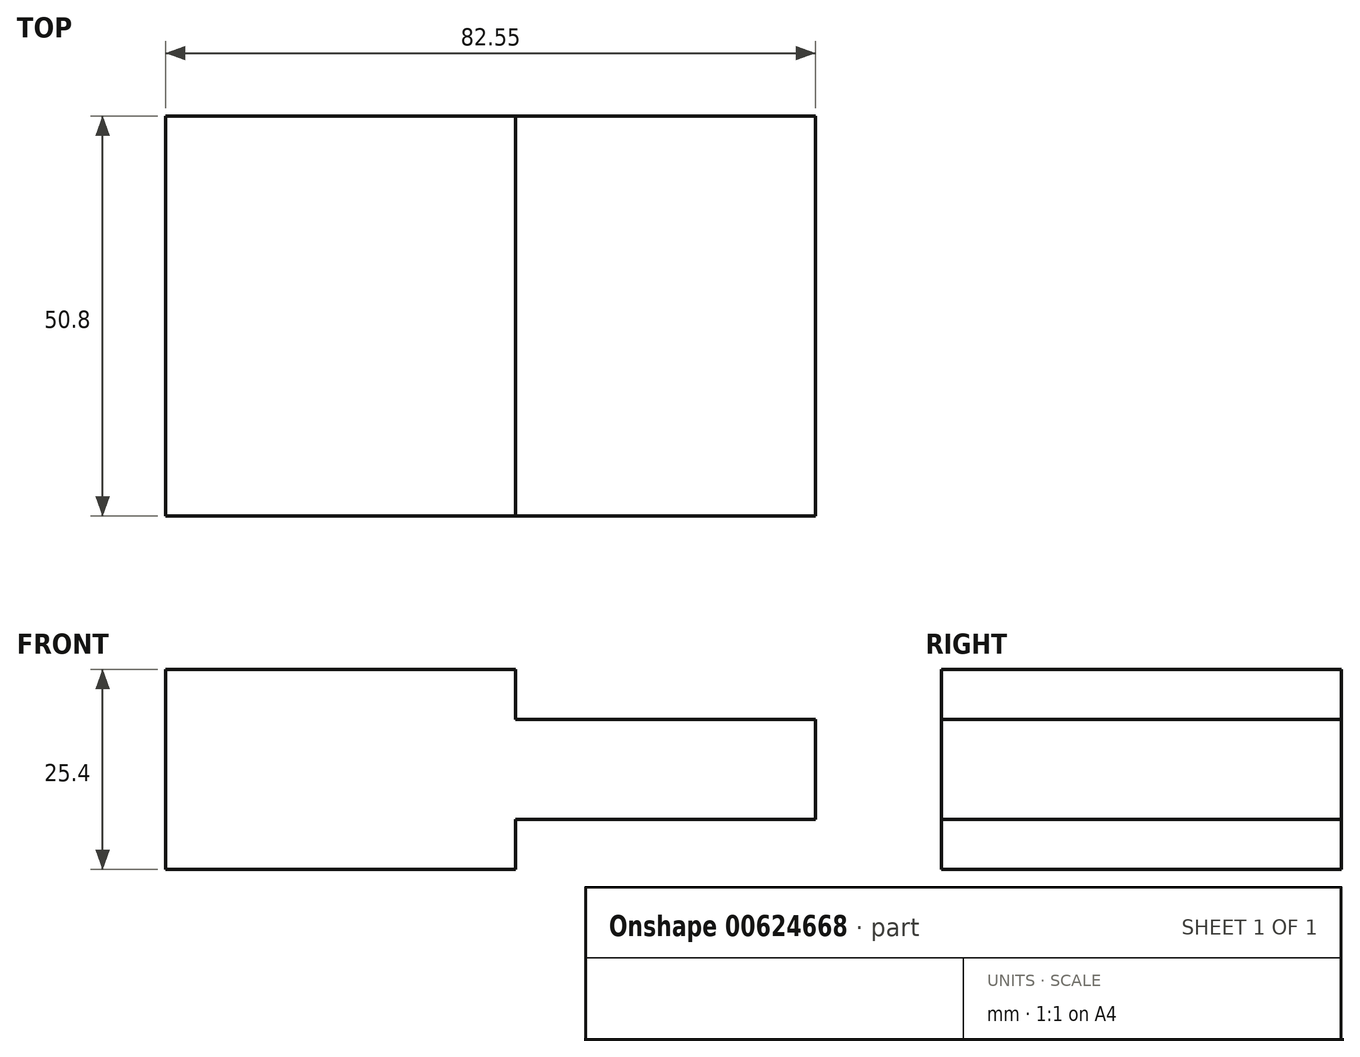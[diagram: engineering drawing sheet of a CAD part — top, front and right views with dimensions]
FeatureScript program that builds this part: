
annotation { "Feature Type Name" : "Feature", "Feature Type Description" : "" }
export const myFeature = defineFeature(function(context is Context, id is Id, definition is map)
    precondition{}
    {
        {
            var Q0;
            Q0=qCreatedBy(makeId("Front.planeOp"),FACE);
            var sketch = newSketch(context, id + "F0", { "sketchPlane" : qUnion([Q0])});
            skLineSegment(sketch, "E0", {"start": v(-48.84, -1.5) * mm, "end": v(-4.39, -1.5) * mm});
            skLineSegment(sketch, "E1", {"start": v(-4.39, 4.86) * mm, "end": v(33.71, 4.86) * mm});
            skLineSegment(sketch, "E2", {"start": v(33.71, 4.86) * mm, "end": v(33.71, 17.56) * mm});
            skLineSegment(sketch, "E3", {"start": v(33.71, 17.56) * mm, "end": v(-4.39, 17.56) * mm});
            skLineSegment(sketch, "E4", {"start": v(-4.39, 17.56) * mm, "end": v(-4.39, 23.9) * mm});
            skLineSegment(sketch, "E5", {"start": v(-4.39, 23.9) * mm, "end": v(-48.84, 23.9) * mm});
            skLineSegment(sketch, "E6", {"start": v(-4.39, -1.5) * mm, "end": v(-4.39, 4.86) * mm});
            skLineSegment(sketch, "E7", {"start": v(-48.84, 23.9) * mm, "end": v(-48.84, -1.5) * mm});
            skSolve(sketch);
        }
        {
            var Q0;
            Q0=makeQuery(id+"F0.imprint","IMPRINT",FACE,{"disambiguationData":[TD([[makeQuery(id+"F0.imprint","IMPRINT",EDGE,{"derivedFrom":sQuery(id+"F0.wireOp",EDGE,"E0")}),1.0]])]});
            extrude(context, id + "F1", {"entities" : qUnion([Q0]), "depth" : 50.8 * mm, "offsetDistance" : 25.4 * mm});
        }
    });
